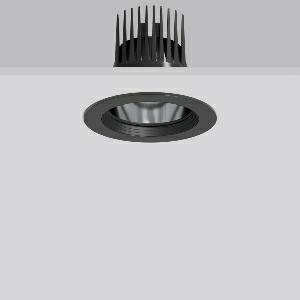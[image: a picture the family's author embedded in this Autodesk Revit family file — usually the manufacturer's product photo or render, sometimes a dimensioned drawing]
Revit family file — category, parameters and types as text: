
# Revit family: heledon_maxi_e_901757_003_1_951b
name_source: partatom
category: Lighting Fixtures
units: mm (PartAtom-declared; Revit-internal decimal feet)

## family parameters
Cut with Voids When Loaded = No
Host = Face
Light Source = No
Part Type = Normal
Room Calculation Point = No
Round Connector Dimension = Use Diameter
Shared = No

## types (1)
- HELEDON maxi E (1 x LED Modul 940, 3500 lm, 4000)
    Apparent Load = 25 VA
    Approval mark = CE
    CIE Flux Codes = 100 100 100 100 100
    Color Rendering = 92
    Color Temperature = 4000
    Default Elevation = 1800 mm
    Description = Series: HELEDON maxi
Round recessed downlight. Housing: die-cast aluminium, powder-coated. Black plastic ring and recessed LED to prevent glare from the side. Optical assembly with reflector made of MIRO-Silver with 98% total light reflection for outstanding efficiency - can be changed without tools. Best colour rendering index Ra>90. Suitable for Recessed ceiling mounting. Installation without tools thanks to spring fastening system. Including separate LED converter with connecting cable 600 mm.High quality converter without flickering and stroboscopic effect. Through-wiring box (5 pole) available as accessory. The following accessories can be mounted without use of tools: interchangeable lenses, decorative glasses, honeycomb louvre, clear and frosted diffusers, white interchangeable plastic ring. 
Colour: deep black, matt (RAL 9005)
Diameter: 162 mm
Height: 3 mm
Cut-out diameter: 152 mm
Recess height: 200 mm
Luminaire: recess height: 135 mm
Lamp: LED
Socket: without socket
Colour temperature: 4000K
Colour rendering index (CRI): 92
System power: 25 W
Rated luminous flux: 3500 lm
Luminous efficiency: 140 lm/W
Control gear: Regulated power supply
Protection class: II
Type of protection: IP 20
    Height = 0 mm  [stored 0 ft]
    Lamp = 1 x LED Modul 940
    Lamp Light Flux = 3500 lm
    Lamp count = 1
    Length = 162 mm
    Lifetime = 50000 h
    Luminous efficacy = 140 lm/W
    Manufacturer = RZB
    ModVariant = No
    Model = 901757.003.1
    Mounting Place = Ceiling
    Mounting Type = Recessed
    Number of Poles = 1
    OnlyDefault = Yes
    Power Factor = 1
    Product Name = HELEDON maxi E
    Product group = Recessed downlights
    ProductGroupID = 402
    Protection Class = Protection class II
    Protection Degree = IP 20
    RLX_Detail_Level = 1
    RLX_Emergency_Light_Flux = 0 lm
    RLX_Emergency_Type = 0
    RLX_Emergency_Type_DB = No
    RlxData = <blob elided: 125501 chars, md5=dee098d6>
    Socket = socket
    Standby Power = 0 W
    System Light Flux = 3500 lm
    System Power = 25 W
    Type Comments = Product without accessories
    Type Image = 901662.003.jpg
    URL = http://relux.com
    VarID = ---
    Voltage = 230 V
    Voltage Range = 220-240 V
    Weight = 0.00 kg
    Width = 0 mm  [stored 0 ft]

note: [stored X ft] marks values corroborated as IEEE doubles in the binary element streams (Revit-internal decimal feet)

## geometry (parser evidence)
native form markers: Blend x4, Sweep x11
no freeform markers — native parametric forms only
